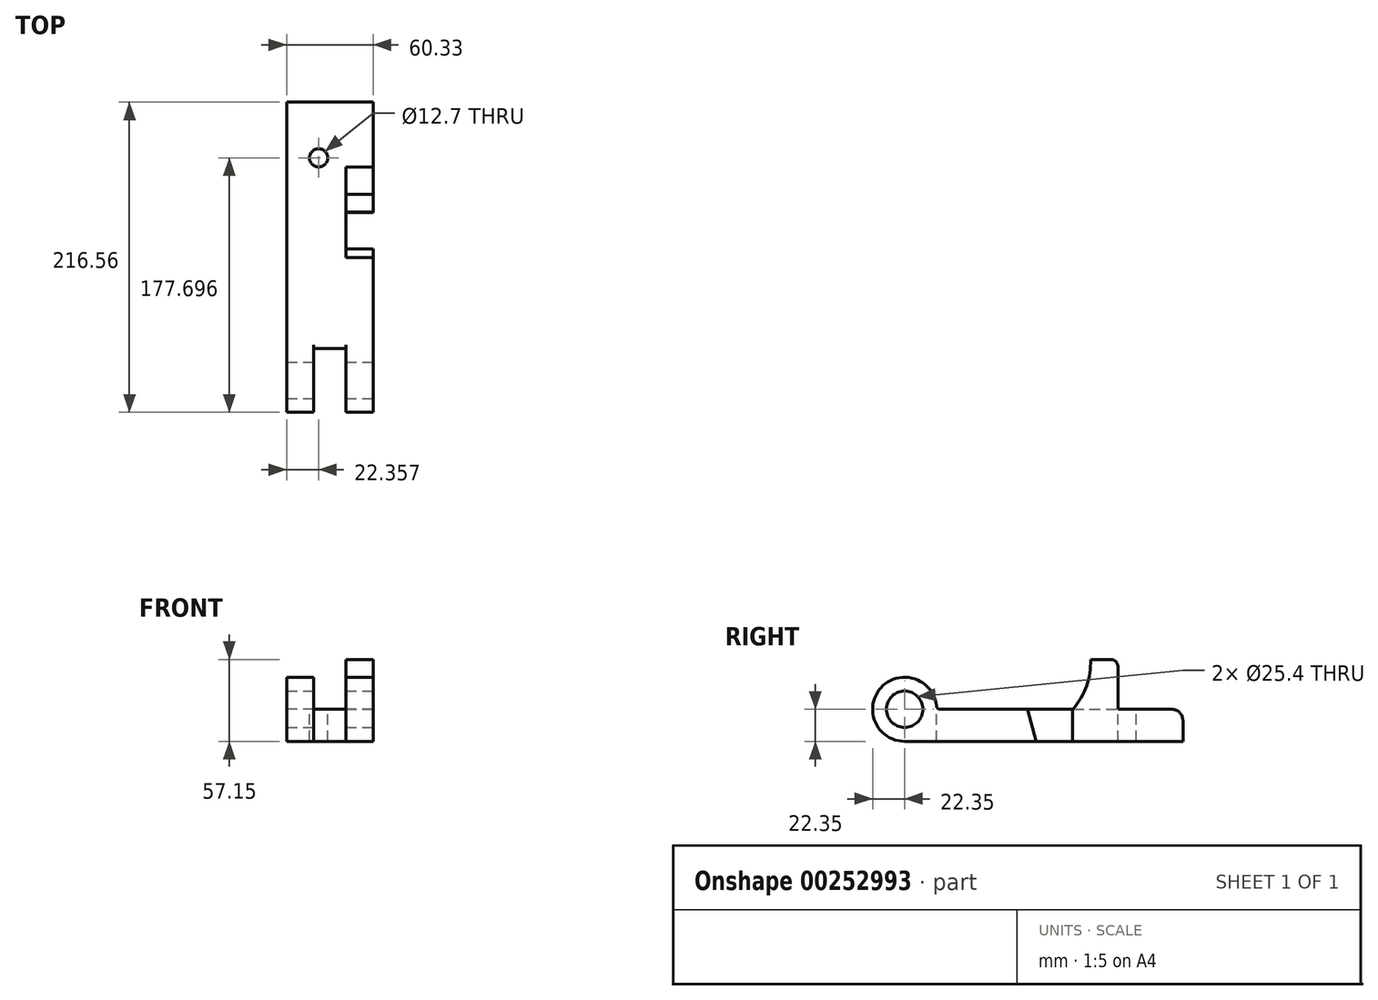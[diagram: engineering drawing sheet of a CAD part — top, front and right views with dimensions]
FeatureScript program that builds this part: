
annotation { "Feature Type Name" : "Feature", "Feature Type Description" : "" }
export const myFeature = defineFeature(function(context is Context, id is Id, definition is map)
    precondition{}
    {
        {
            var Q0;
            Q0=qCreatedBy(makeId("Right.planeOp"),FACE);
            var sketch = newSketch(context, id + "F0", { "sketchPlane" : qUnion([Q0])});
            skCircle(sketch, "E0", {"center": v(0, 0) * mm, "radius": 12.7 * mm});
            skArc(sketch, "E1", {"start": v(22.35, 0) * mm, "mid": v(-15.8, 15.8) * mm, "end": v(0, -22.35) * mm});
            skLineSegment(sketch, "E2", {"start": v(0, 0) * mm, "end": v(0, -22.35) * mm});
            skLineSegment(sketch, "E3", {"start": v(0, -22.35) * mm, "end": v(194.2, -22.35) * mm});
            skLineSegment(sketch, "E4", {"start": v(194.2, -22.35) * mm, "end": v(194.2, 0) * mm});
            skLineSegment(sketch, "E5", {"start": v(194.2, 0) * mm, "end": v(22.35, 0) * mm});
            skSolve(sketch);
        }
        {
            var Q0;
            Q0=makeQuery(id+"F0.imprint","IMPRINT",FACE,{"disambiguationData":[TD([[makeQuery(id+"F0.imprint","IMPRINT",EDGE,{"derivedFrom":sQuery(id+"F0.wireOp",EDGE,"E0")}),-1.0]])]});
            extrude(context, id + "F1", {"entities" : qUnion([Q0]), "oppositeDirection" : true, "depth" : 19 * mm});
        }
        {
            var Q0;
            Q0=qCreatedBy(makeId("Top.planeOp"),FACE);
            var sketch = newSketch(context, id + "F2", { "sketchPlane" : qUnion([Q0])});
            skLineSegment(sketch, "E6.0", {"start": v(-19, 194.2) * mm, "end": v(-19, 22.35) * mm});
            skLineSegment(sketch, "E7", {"start": v(-19, 22.35) * mm, "end": v(-41.33, 22.35) * mm});
            skLineSegment(sketch, "E8", {"start": v(-41.33, 22.35) * mm, "end": v(-41.33, 194.2) * mm});
            skLineSegment(sketch, "E9", {"start": v(-41.33, 194.2) * mm, "end": v(-19, 194.2) * mm});
            skSolve(sketch);
        }
        {
            var Q0;
            Q0=qSketchRegion(id+"F2",true);
            extrude(context, id + "F3", {"entities" : qUnion([Q0]), "operationType" : NewBodyOperationType.ADD, "oppositeDirection" : true, "depth" : 22.35 * mm});
        }
        {
            var Q0;
            Q0=qCreatedBy(makeId("Right.planeOp"),FACE);
            cPlane(context, id + "F4", {"entities" : qUnion([Q0]), "cplaneType" : CPlaneType.OFFSET, "offset" : 41.33 * mm, "oppositeDirection" : true, "width" : 152.4 * mm, "height" : 152.4 * mm});
        }
        {
            var Q0;
            Q0=qCreatedBy(id+"F4.planeOp",FACE);
            var sketch = newSketch(context, id + "F5", { "sketchPlane" : qUnion([Q0])});
            skArc(sketch, "E10.0", {"start": v(22.35, 0) * mm, "mid": v(-15.8, 15.8) * mm, "end": v(0, -22.35) * mm});
            skLineSegment(sketch, "E11.0", {"start": v(194.2, 0) * mm, "end": v(22.35, 0) * mm});
            skLineSegment(sketch, "E12.0", {"start": v(0, -22.35) * mm, "end": v(194.2, -22.35) * mm});
            skLineSegment(sketch, "E13.0", {"start": v(194.2, -22.35) * mm, "end": v(194.2, 0) * mm});
            skCircle(sketch, "E14.0", {"center": v(0, 0) * mm, "radius": 12.7 * mm});
            skSolve(sketch);
        }
        {
            var Q0;
            Q0=qSketchRegion(id+"F5",true);
            extrude(context, id + "F6", {"entities" : qUnion([Q0]), "operationType" : NewBodyOperationType.ADD, "oppositeDirection" : true, "depth" : 19 * mm});
        }
        {
            var Q0;
            Q0=qCreatedBy(makeId("Right.planeOp"),FACE);
            var sketch = newSketch(context, id + "F7", { "sketchPlane" : qUnion([Q0])});
            skPoint(sketch, "E15.0", {"position": v(0, 0) * mm});
            skCircle(sketch, "E16.0", {"center": v(0, 0) * mm, "radius": 12.7 * mm});
            skArc(sketch, "E17.0", {"start": v(22.35, 0) * mm, "mid": v(-15.8, 15.8) * mm, "end": v(0, -22.35) * mm});
            skLineSegment(sketch, "E18.0", {"start": v(194.2, 0) * mm, "end": v(22.35, 0) * mm});
            skLineSegment(sketch, "E19.0", {"start": v(0, -22.35) * mm, "end": v(194.2, -22.35) * mm});
            skLineSegment(sketch, "E20.0", {"start": v(194.2, -22.35) * mm, "end": v(194.2, 0) * mm});
            skLineSegment(sketch, "E21", {"start": v(0, -22.35) * mm, "end": v(91.85, -22.35) * mm});
            skLineSegment(sketch, "E22", {"start": v(0, 0) * mm, "end": v(85.85, 0) * mm});
            skLineSegment(sketch, "E23", {"start": v(0, -22.35) * mm, "end": v(117.25, -22.35) * mm});
            skLineSegment(sketch, "E24", {"start": v(117.25, -22.35) * mm, "end": v(117.25, 0) * mm});
            skLineSegment(sketch, "E25", {"start": v(117.25, 0) * mm, "end": v(85.85, 0) * mm});
            skLineSegment(sketch, "E26", {"start": v(85.85, 0) * mm, "end": v(91.85, -22.35) * mm});
            skSolve(sketch);
        }
        {
            var Q0;
            {var subQ0=sQuery(id+"F7.wireOp",EDGE,"E24");Q0=makeQuery(id+"F7.imprint","IMPRINT",FACE,{"disambiguationData":[TD([[makeQuery(id+"F7.imprint","IMPRINT",EDGE,{"derivedFrom":subQ0}),1.0]])]});}
            extrude(context, id + "F8", {"entities" : qUnion([Q0]), "operationType" : NewBodyOperationType.REMOVE, "oppositeDirection" : true, "depth" : 19.05 * mm});
        }
        {
            var Q0;
            Q0=qCreatedBy(makeId("Right.planeOp"),FACE);
            var sketch = newSketch(context, id + "F9", { "sketchPlane" : qUnion([Q0])});
            skArc(sketch, "E27.0", {"start": v(22.35, 0) * mm, "mid": v(-15.8, 15.8) * mm, "end": v(0, -22.35) * mm});
            skCircle(sketch, "E28.0", {"center": v(0, 0) * mm, "radius": 12.7 * mm});
            skLineSegment(sketch, "E29", {"start": v(0, 0) * mm, "end": v(148.82, 0) * mm});
            skLineSegment(sketch, "E30", {"start": v(148.82, 0) * mm, "end": v(148.82, 34.8) * mm});
            skLineSegment(sketch, "E31", {"start": v(148.82, 34.8) * mm, "end": v(129.77, 34.8) * mm});
            skArc(sketch, "E32", {"start": v(117.53, 0) * mm, "mid": v(126.92, 16.25) * mm, "end": v(129.77, 34.8) * mm});
            skSolve(sketch);
        }
        {
            var Q0;
            {var subQ0=sQuery(id+"F9.wireOp",EDGE,"E30");Q0=makeQuery(id+"F9.imprint","IMPRINT",FACE,{"disambiguationData":[TD([[makeQuery(id+"F9.imprint","IMPRINT",EDGE,{"derivedFrom":subQ0}),1.0]])]});}
            extrude(context, id + "F10", {"entities" : qUnion([Q0]), "operationType" : NewBodyOperationType.ADD, "oppositeDirection" : true, "depth" : 19.05 * mm});
        }
        {
            var Q0;
            Q0=makeQuery(id+"F6.boolean.opBoolean","MERGE",FACE,{"derivedFrom":[makeQuery(id+"F3.boolean.opBoolean","MERGE",FACE,{"derivedFrom":[makeQuery(id+"F1.opExtrude","SWEPT_FACE",FACE,{"disambiguationData":[OSD([sQuery(id+"F0.wireOp",EDGE,"E5")])]}),makeQuery(id+"F3.opExtrude","CAP_FACE",FACE,{"disambiguationData":[OSD([sQuery(id+"F2.wireOp",EDGE,"E6.0"),sQuery(id+"F2.wireOp",EDGE,"E7"),sQuery(id+"F2.wireOp",EDGE,"E8"),sQuery(id+"F2.wireOp",EDGE,"E9")])],"isStart":true})]}),makeQuery(id+"F6.opExtrude","SWEPT_FACE",FACE,{"disambiguationData":[OSD([sQuery(id+"F5.wireOp",EDGE,"E11.0")])]})]});
            var sketch = newSketch(context, id + "F11", { "sketchPlane" : qUnion([Q0])});
            skLineSegment(sketch, "E33.0", {"start": v(-60.33, 194.2) * mm, "end": v(-60.33, 22.35) * mm});
            skLineSegment(sketch, "E34.0", {"start": v(-60.33, 194.2) * mm, "end": v(0, 194.2) * mm});
            skCircle(sketch, "E35", {"center": v(-37.97, 155.35) * mm, "radius": 6.35 * mm});
            skSolve(sketch);
        }
        {
            var Q0;
            Q0=qSketchRegion(id+"F11",true);
            extrude(context, id + "F12", {"entities" : qUnion([Q0]), "operationType" : NewBodyOperationType.REMOVE, "endBound" : BoundingType.THROUGH_ALL, "oppositeDirection" : true, "depth" : 25.4 * mm});
        }
        {
            var Q0;
            Q0=makeQuery(id+"F10.opExtrude","SWEPT_EDGE",EDGE,{"disambiguationData":[OSD([sQuery(id+"F9.wireOp",EDGE,"E30"),sQuery(id+"F9.wireOp",EDGE,"E31")])]});
            fillet(context, id + "F13", {"entities" : qUnion([Q0]), "radius" : 5.08 * mm, "tangentPropagation" : true, "allowEdgeOverflow" : false});
        }
        {
            var Q0;
            Q0=makeQuery(id+"F6.boolean.opBoolean","MERGE",EDGE,{"derivedFrom":[makeQuery(id+"F3.boolean.opBoolean","MERGE",EDGE,{"derivedFrom":[makeQuery(id+"F1.opExtrude","SWEPT_EDGE",EDGE,{"disambiguationData":[OSD([sQuery(id+"F0.wireOp",EDGE,"E4"),sQuery(id+"F0.wireOp",EDGE,"E5")])]}),makeQuery(id+"F3.opExtrude","CAP_EDGE",EDGE,{"disambiguationData":[OSD([sQuery(id+"F2.wireOp",EDGE,"E9")])],"isStart":true})]}),makeQuery(id+"F6.opExtrude","SWEPT_EDGE",EDGE,{"disambiguationData":[OSD([sQuery(id+"F5.wireOp",EDGE,"E11.0"),sQuery(id+"F5.wireOp",EDGE,"E13.0")])]})]});
            fillet(context, id + "F14", {"entities" : qUnion([Q0]), "radius" : 7.87 * mm, "tangentPropagation" : true, "allowEdgeOverflow" : false});
        }
        {
            var Q0;
            Q0=makeQuery(id+"F1.opExtrude","SWEPT_EDGE",EDGE,{"disambiguationData":[OSD([sQuery(id+"F0.wireOp",EDGE,"E1"),sQuery(id+"F0.wireOp",EDGE,"E5")])]});
            var Q1;
            Q1=makeQuery(id+"F6.opExtrude","SWEPT_EDGE",EDGE,{"disambiguationData":[OSD([sQuery(id+"F5.wireOp",EDGE,"E10.0"),sQuery(id+"F5.wireOp",EDGE,"E11.0")])]});
            fillet(context, id + "F15", {"entities" : qUnion([Q0, Q1]), "radius" : 2.54 * mm, "tangentPropagation" : true, "allowEdgeOverflow" : false});
        }
    });
